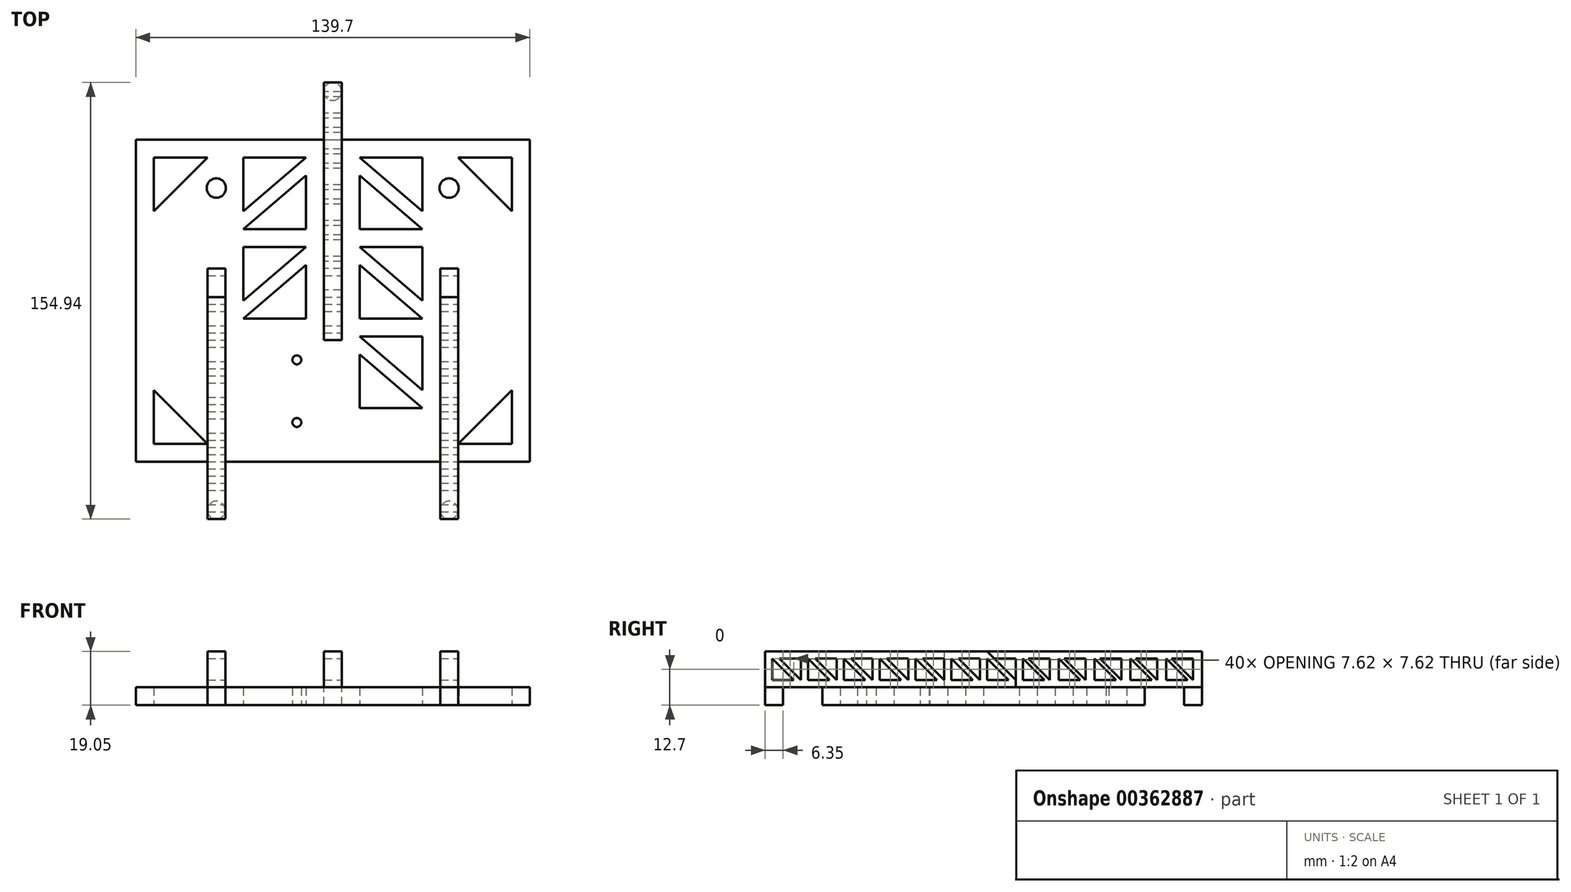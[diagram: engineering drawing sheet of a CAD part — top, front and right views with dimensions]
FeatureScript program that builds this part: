
annotation { "Feature Type Name" : "Feature", "Feature Type Description" : "" }
export const myFeature = defineFeature(function(context is Context, id is Id, definition is map)
    precondition{}
    {
        {
            var Q0;
            Q0=qCreatedBy(makeId("Top.planeOp"),FACE);
            var sketch = newSketch(context, id + "F0", { "sketchPlane" : qUnion([Q0])});
            skLineSegment(sketch, "E0.bottom", {"start": v(-69.85, 57.15) * mm, "end": v(69.85, 57.15) * mm});
            skLineSegment(sketch, "E0.top", {"start": v(-69.85, -57.15) * mm, "end": v(69.85, -57.15) * mm});
            skLineSegment(sketch, "E0.left", {"start": v(-69.85, 57.15) * mm, "end": v(-69.85, -57.15) * mm});
            skLineSegment(sketch, "E0.right", {"start": v(69.85, 57.15) * mm, "end": v(69.85, -57.15) * mm});
            skPoint(sketch, "E0.middle", {"position": v(0, 0) * mm});
            skCircle(sketch, "E1", {"center": v(-41.28, 40) * mm, "radius": 3.43 * mm});
            skCircle(sketch, "E2.MirrorC", {"center": v(41.28, 40) * mm, "radius": 3.43 * mm});
            skCircle(sketch, "E3", {"center": v(-12.7, -43.18) * mm, "radius": 1.59 * mm});
            skCircle(sketch, "E4", {"center": v(-12.7, -20.95) * mm, "radius": 1.59 * mm});
            skLineSegment(sketch, "E5", {"start": v(-63.5, 50.8) * mm, "end": v(-63.5, 31.75) * mm});
            skLineSegment(sketch, "E6", {"start": v(-63.5, 31.75) * mm, "end": v(-44.45, 50.8) * mm});
            skLineSegment(sketch, "E7", {"start": v(-44.45, 50.8) * mm, "end": v(-63.5, 50.8) * mm});
            skLineSegment(sketch, "E8.MirrorCS", {"start": v(63.5, 50.8) * mm, "end": v(63.5, 31.75) * mm});
            skLineSegment(sketch, "E9.MirrorCS", {"start": v(44.45, 50.8) * mm, "end": v(63.5, 50.8) * mm});
            skLineSegment(sketch, "E10.MirrorCS", {"start": v(63.5, 31.75) * mm, "end": v(44.45, 50.8) * mm});
            skLineSegment(sketch, "E11.MirrorCS", {"start": v(-63.5, -50.8) * mm, "end": v(-63.5, -31.75) * mm});
            skLineSegment(sketch, "E12.MirrorCS", {"start": v(-63.5, -31.75) * mm, "end": v(-44.45, -50.8) * mm});
            skLineSegment(sketch, "E13.MirrorCS", {"start": v(-44.45, -50.8) * mm, "end": v(-63.5, -50.8) * mm});
            skLineSegment(sketch, "E14.MirrorCS", {"start": v(44.45, -50.8) * mm, "end": v(63.5, -50.8) * mm});
            skLineSegment(sketch, "E15.MirrorCS", {"start": v(63.5, -31.75) * mm, "end": v(44.45, -50.8) * mm});
            skLineSegment(sketch, "E16.MirrorCS", {"start": v(63.5, -50.8) * mm, "end": v(63.5, -31.75) * mm});
            skLineSegment(sketch, "E17", {"start": v(-31.75, 50.8) * mm, "end": v(-31.75, 31.75) * mm});
            skLineSegment(sketch, "E18", {"start": v(-31.75, 31.75) * mm, "end": v(-9.53, 50.8) * mm});
            skLineSegment(sketch, "E19", {"start": v(-9.52, 50.8) * mm, "end": v(-31.75, 50.8) * mm});
            skLineSegment(sketch, "E20", {"start": v(-31.75, 25.4) * mm, "end": v(-9.52, 44.45) * mm});
            skLineSegment(sketch, "E21", {"start": v(-9.53, 44.45) * mm, "end": v(-9.53, 25.4) * mm});
            skLineSegment(sketch, "E22", {"start": v(-9.52, 25.4) * mm, "end": v(-31.75, 25.4) * mm});
            skLineSegment(sketch, "E23.0.1.0", {"start": v(-31.75, 0) * mm, "end": v(-9.53, 19.05) * mm});
            skLineSegment(sketch, "E23.0.1.1", {"start": v(-31.75, 19.05) * mm, "end": v(-31.75, 0) * mm});
            skLineSegment(sketch, "E23.0.1.2", {"start": v(-9.52, 19.05) * mm, "end": v(-31.75, 19.05) * mm});
            skLineSegment(sketch, "E23.0.1.3", {"start": v(-31.75, -6.35) * mm, "end": v(-9.52, 12.7) * mm});
            skLineSegment(sketch, "E23.0.1.4", {"start": v(-9.53, 12.7) * mm, "end": v(-9.53, -6.35) * mm});
            skLineSegment(sketch, "E23.0.1.5", {"start": v(-9.52, -6.35) * mm, "end": v(-31.75, -6.35) * mm});
            skLineSegment(sketch, "E23.direction1", {"start": v(-31.75, 31.75) * mm, "end": v(-6.35, 31.75) * mm, "construction": true});
            skLineSegment(sketch, "E23.direction2", {"start": v(-31.75, 31.75) * mm, "end": v(-31.75, 0) * mm, "construction": true});
            skLineSegment(sketch, "E24.MirrorCS", {"start": v(31.75, 31.75) * mm, "end": v(9.53, 50.8) * mm});
            skLineSegment(sketch, "E25.MirrorCS", {"start": v(31.75, 50.8) * mm, "end": v(31.75, 31.75) * mm});
            skLineSegment(sketch, "E26.MirrorCS", {"start": v(9.52, 50.8) * mm, "end": v(31.75, 50.8) * mm});
            skLineSegment(sketch, "E27.MirrorCS", {"start": v(31.75, 25.4) * mm, "end": v(9.52, 44.45) * mm});
            skLineSegment(sketch, "E28.MirrorCS", {"start": v(9.53, 44.45) * mm, "end": v(9.53, 25.4) * mm});
            skLineSegment(sketch, "E29.MirrorCS", {"start": v(9.52, 25.4) * mm, "end": v(31.75, 25.4) * mm});
            skLineSegment(sketch, "E30.0.1.0", {"start": v(31.75, -6.35) * mm, "end": v(9.52, 12.7) * mm});
            skLineSegment(sketch, "E30.0.1.1", {"start": v(9.53, 12.7) * mm, "end": v(9.53, -6.35) * mm});
            skLineSegment(sketch, "E30.0.1.2", {"start": v(9.52, -6.35) * mm, "end": v(31.75, -6.35) * mm});
            skLineSegment(sketch, "E30.0.1.3", {"start": v(31.75, 0) * mm, "end": v(9.53, 19.05) * mm});
            skLineSegment(sketch, "E30.0.1.4", {"start": v(9.52, 19.05) * mm, "end": v(31.75, 19.05) * mm});
            skLineSegment(sketch, "E30.0.1.5", {"start": v(31.75, 19.05) * mm, "end": v(31.75, 0) * mm});
            skLineSegment(sketch, "E30.0.2.0", {"start": v(31.75, -38.1) * mm, "end": v(9.52, -19.05) * mm});
            skLineSegment(sketch, "E30.0.2.1", {"start": v(9.53, -19.05) * mm, "end": v(9.53, -38.1) * mm});
            skLineSegment(sketch, "E30.0.2.2", {"start": v(9.52, -38.1) * mm, "end": v(31.75, -38.1) * mm});
            skLineSegment(sketch, "E30.0.2.3", {"start": v(31.75, -31.75) * mm, "end": v(9.53, -12.7) * mm});
            skLineSegment(sketch, "E30.0.2.4", {"start": v(9.52, -12.7) * mm, "end": v(31.75, -12.7) * mm});
            skLineSegment(sketch, "E30.0.2.5", {"start": v(31.75, -12.7) * mm, "end": v(31.75, -31.75) * mm});
            skLineSegment(sketch, "E30.direction1", {"start": v(9.52, 25.4) * mm, "end": v(34.92, 25.4) * mm, "construction": true});
            skLineSegment(sketch, "E30.direction2", {"start": v(9.52, 25.4) * mm, "end": v(9.52, -6.35) * mm, "construction": true});
            skSolve(sketch);
        }
        {
            var Q0;
            Q0=makeQuery(id+"F0.imprint","IMPRINT",FACE,{"disambiguationData":[TD([[makeQuery(id+"F0.imprint","IMPRINT",EDGE,{"derivedFrom":sQuery(id+"F0.wireOp",EDGE,"E0.bottom")}),-1.0]])]});
            extrude(context, id + "F1", {"entities" : qUnion([Q0]), "depth" : 6.35 * mm});
        }
        {
            var Q0;
            Q0=makeQuery(id+"F1.opExtrude","CAP_FACE",FACE,{"disambiguationData":[OSD([sQuery(id+"F0.wireOp",EDGE,"E0.bottom"),sQuery(id+"F0.wireOp",EDGE,"E0.top"),sQuery(id+"F0.wireOp",EDGE,"E0.left"),sQuery(id+"F0.wireOp",EDGE,"E0.right"),sQuery(id+"F0.wireOp",EDGE,"E1"),sQuery(id+"F0.wireOp",EDGE,"E2.MirrorC")])],"isStart":false});
            var sketch = newSketch(context, id + "F2", { "sketchPlane" : qUnion([Q0])});
            skLineSegment(sketch, "E31.bottom", {"start": v(-38.1, -77.47) * mm, "end": v(-44.45, -77.47) * mm});
            skLineSegment(sketch, "E31.top", {"start": v(-38.1, 11.43) * mm, "end": v(-44.45, 11.43) * mm});
            skLineSegment(sketch, "E31.left", {"start": v(-38.1, -77.47) * mm, "end": v(-38.1, 11.43) * mm});
            skLineSegment(sketch, "E31.right", {"start": v(-44.45, -77.47) * mm, "end": v(-44.45, 11.43) * mm});
            skPoint(sketch, "E31.middle", {"position": v(-41.27, -33.02) * mm});
            skLineSegment(sketch, "E32.MirrorCS", {"start": v(44.45, -77.47) * mm, "end": v(44.45, 11.43) * mm});
            skLineSegment(sketch, "E33.MirrorCS", {"start": v(38.1, -77.47) * mm, "end": v(38.1, 11.43) * mm});
            skLineSegment(sketch, "E34.MirrorCS", {"start": v(38.1, 11.43) * mm, "end": v(44.45, 11.43) * mm});
            skLineSegment(sketch, "E35.MirrorCS", {"start": v(38.1, -77.47) * mm, "end": v(44.45, -77.47) * mm});
            skLineSegment(sketch, "E36.bottom", {"start": v(-3.17, 77.47) * mm, "end": v(3.18, 77.47) * mm});
            skLineSegment(sketch, "E36.top", {"start": v(-3.17, -13.97) * mm, "end": v(3.18, -13.97) * mm});
            skLineSegment(sketch, "E36.left", {"start": v(-3.17, 77.47) * mm, "end": v(-3.17, -13.97) * mm});
            skLineSegment(sketch, "E36.right", {"start": v(3.18, 77.47) * mm, "end": v(3.18, -13.97) * mm});
            skPoint(sketch, "E36.middle", {"position": v(0, 31.75) * mm});
            skSolve(sketch);
        }
        {
            var Q0;
            {var subQ0=sQuery(id+"F2.wireOp",EDGE,"E31.top");Q0=makeQuery(id+"F2.imprint","IMPRINT",FACE,{"disambiguationData":[TD([[makeQuery(id+"F2.imprint","IMPRINT",EDGE,{"derivedFrom":subQ0}),1.0]])]});}
            var Q1;
            {var subQ0=sQuery(id+"F2.wireOp",EDGE,"E31.bottom");Q1=makeQuery(id+"F2.imprint","IMPRINT",FACE,{"disambiguationData":[TD([[makeQuery(id+"F2.imprint","IMPRINT",EDGE,{"derivedFrom":subQ0}),-1.0]])]});}
            var Q2;
            {var subQ0=sQuery(id+"F2.wireOp",EDGE,"E35.MirrorCS");Q2=makeQuery(id+"F2.imprint","IMPRINT",FACE,{"disambiguationData":[TD([[makeQuery(id+"F2.imprint","IMPRINT",EDGE,{"derivedFrom":subQ0}),1.0]])]});}
            var Q3;
            {var subQ0=sQuery(id+"F2.wireOp",EDGE,"E34.MirrorCS");Q3=makeQuery(id+"F2.imprint","IMPRINT",FACE,{"disambiguationData":[TD([[makeQuery(id+"F2.imprint","IMPRINT",EDGE,{"derivedFrom":subQ0}),-1.0]])]});}
            var Q4;
            {var subQ0=sQuery(id+"F2.wireOp",EDGE,"E36.top");Q4=makeQuery(id+"F2.imprint","IMPRINT",FACE,{"disambiguationData":[TD([[makeQuery(id+"F2.imprint","IMPRINT",EDGE,{"derivedFrom":subQ0}),1.0]])]});}
            var Q5;
            {var subQ0=sQuery(id+"F2.wireOp",EDGE,"E36.bottom");Q5=makeQuery(id+"F2.imprint","IMPRINT",FACE,{"disambiguationData":[TD([[makeQuery(id+"F2.imprint","IMPRINT",EDGE,{"derivedFrom":subQ0}),-1.0]])]});}
            extrude(context, id + "F3", {"entities" : qUnion([Q0, Q1, Q2, Q3, Q4, Q5]), "operationType" : NewBodyOperationType.ADD, "depth" : 12.7 * mm});
        }
        {
            var Q0;
            Q0=makeQuery(id+"F3.opExtrude","CAP_FACE",FACE,{"disambiguationData":[OSD([sQuery(id+"F2.wireOp",EDGE,"E31.bottom"),sQuery(id+"F2.wireOp",EDGE,"E31.top"),sQuery(id+"F2.wireOp",EDGE,"E31.left"),sQuery(id+"F2.wireOp",EDGE,"E31.right")])],"isStart":true});
            var sketch = newSketch(context, id + "F4", { "sketchPlane" : qUnion([Q0])});
            skCircle(sketch, "E37", {"center": v(-41.27, 74.3) * mm, "radius": 3.18 * mm});
            skCircle(sketch, "E38", {"center": v(41.27, 74.3) * mm, "radius": 3.18 * mm});
            skCircle(sketch, "E39", {"center": v(0, -74.3) * mm, "radius": 3.18 * mm});
            skSolve(sketch);
        }
        {
            var Q0;
            {var subQ0=sQuery(id+"F4.wireOp",EDGE,"E37");var subQ1=sQuery(id+"F2.wireOp",EDGE,"E31.bottom");var subQ2=makeQuery(id+"F4.imprint","INTERSECT",VERTEX,{"derivedFrom":[makeQuery(id+"F3.opExtrude","CAP_EDGE",EDGE,{"disambiguationData":[OSD([subQ1])],"isStart":true}),subQ0]});Q0=makeQuery(id+"F4.imprint","IMPRINT",FACE,{"disambiguationData":[TD([[makeQuery(id+"F4.imprint","IMPRINT",EDGE,{"disambiguationData":[TD([[subQ2,1.0]])],"derivedFrom":subQ0}),1.0]])]});}
            var Q1;
            Q1=makeQuery(id+"F4.imprint","IMPRINT",FACE,{"disambiguationData":[TD([[makeQuery(id+"F4.imprint","IMPRINT",EDGE,{"derivedFrom":sQuery(id+"F4.wireOp",EDGE,"E38")}),1.0]])]});
            var Q2;
            Q2=makeQuery(id+"F4.imprint","IMPRINT",FACE,{"disambiguationData":[TD([[makeQuery(id+"F4.imprint","IMPRINT",EDGE,{"derivedFrom":sQuery(id+"F4.wireOp",EDGE,"E39")}),1.0]])]});
            extrude(context, id + "F5", {"entities" : qUnion([Q0, Q1, Q2]), "operationType" : NewBodyOperationType.ADD, "depth" : 6.35 * mm});
        }
        {
            var Q0;
            Q0=makeQuery(id+"F3.opExtrude","SWEPT_FACE",FACE,{"disambiguationData":[OSD([sQuery(id+"F2.wireOp",EDGE,"E32.MirrorCS")])]});
            var sketch = newSketch(context, id + "F6", { "sketchPlane" : qUnion([Q0])});
            skLineSegment(sketch, "E40", {"start": v(-74.93, 16.51) * mm, "end": v(-74.93, 8.89) * mm});
            skLineSegment(sketch, "E41", {"start": v(-74.93, 8.89) * mm, "end": v(-67.31, 8.89) * mm});
            skLineSegment(sketch, "E42", {"start": v(-67.31, 8.89) * mm, "end": v(-74.93, 16.5) * mm});
            skLineSegment(sketch, "E43", {"start": v(-72.4, 16.51) * mm, "end": v(-64.77, 8.89) * mm});
            skLineSegment(sketch, "E44", {"start": v(-64.77, 8.9) * mm, "end": v(-64.77, 16.51) * mm});
            skLineSegment(sketch, "E45", {"start": v(-64.77, 16.5) * mm, "end": v(-72.4, 16.5) * mm});
            skLineSegment(sketch, "E46.1.0.0", {"start": v(-52.07, 8.9) * mm, "end": v(-52.07, 16.51) * mm});
            skLineSegment(sketch, "E46.1.0.1", {"start": v(-59.7, 16.51) * mm, "end": v(-52.07, 8.9) * mm});
            skLineSegment(sketch, "E46.1.0.2", {"start": v(-52.07, 16.5) * mm, "end": v(-59.7, 16.5) * mm});
            skLineSegment(sketch, "E46.1.0.3", {"start": v(-54.61, 8.89) * mm, "end": v(-62.23, 16.5) * mm});
            skLineSegment(sketch, "E46.1.0.4", {"start": v(-62.23, 16.51) * mm, "end": v(-62.23, 8.89) * mm});
            skLineSegment(sketch, "E46.1.0.5", {"start": v(-62.23, 8.89) * mm, "end": v(-54.61, 8.89) * mm});
            skLineSegment(sketch, "E46.2.0.0", {"start": v(-39.37, 8.9) * mm, "end": v(-39.37, 16.51) * mm});
            skLineSegment(sketch, "E46.2.0.1", {"start": v(-47, 16.51) * mm, "end": v(-39.37, 8.9) * mm});
            skLineSegment(sketch, "E46.2.0.2", {"start": v(-39.37, 16.5) * mm, "end": v(-47, 16.5) * mm});
            skLineSegment(sketch, "E46.2.0.3", {"start": v(-41.91, 8.89) * mm, "end": v(-49.53, 16.5) * mm});
            skLineSegment(sketch, "E46.2.0.4", {"start": v(-49.53, 16.51) * mm, "end": v(-49.53, 8.89) * mm});
            skLineSegment(sketch, "E46.2.0.5", {"start": v(-49.53, 8.89) * mm, "end": v(-41.91, 8.89) * mm});
            skLineSegment(sketch, "E46.3.0.0", {"start": v(-26.67, 8.9) * mm, "end": v(-26.67, 16.51) * mm});
            skLineSegment(sketch, "E46.3.0.1", {"start": v(-34.3, 16.51) * mm, "end": v(-26.67, 8.9) * mm});
            skLineSegment(sketch, "E46.3.0.2", {"start": v(-26.67, 16.5) * mm, "end": v(-34.3, 16.5) * mm});
            skLineSegment(sketch, "E46.3.0.3", {"start": v(-29.21, 8.89) * mm, "end": v(-36.83, 16.5) * mm});
            skLineSegment(sketch, "E46.3.0.4", {"start": v(-36.83, 16.51) * mm, "end": v(-36.83, 8.89) * mm});
            skLineSegment(sketch, "E46.3.0.5", {"start": v(-36.83, 8.89) * mm, "end": v(-29.21, 8.89) * mm});
            skLineSegment(sketch, "E46.4.0.0", {"start": v(-13.97, 8.9) * mm, "end": v(-13.97, 16.51) * mm});
            skLineSegment(sketch, "E46.4.0.1", {"start": v(-21.59, 16.51) * mm, "end": v(-13.97, 8.9) * mm});
            skLineSegment(sketch, "E46.4.0.2", {"start": v(-13.97, 16.5) * mm, "end": v(-21.59, 16.5) * mm});
            skLineSegment(sketch, "E46.4.0.3", {"start": v(-16.51, 8.89) * mm, "end": v(-24.13, 16.5) * mm});
            skLineSegment(sketch, "E46.4.0.4", {"start": v(-24.13, 16.51) * mm, "end": v(-24.13, 8.89) * mm});
            skLineSegment(sketch, "E46.4.0.5", {"start": v(-24.13, 8.89) * mm, "end": v(-16.5, 8.89) * mm});
            skLineSegment(sketch, "E46.5.0.0", {"start": v(-1.27, 8.9) * mm, "end": v(-1.27, 16.51) * mm});
            skLineSegment(sketch, "E46.5.0.1", {"start": v(-8.89, 16.51) * mm, "end": v(-1.27, 8.9) * mm});
            skLineSegment(sketch, "E46.5.0.2", {"start": v(-1.27, 16.5) * mm, "end": v(-8.89, 16.5) * mm});
            skLineSegment(sketch, "E46.5.0.3", {"start": v(-3.81, 8.89) * mm, "end": v(-11.43, 16.5) * mm});
            skLineSegment(sketch, "E46.5.0.4", {"start": v(-11.43, 16.51) * mm, "end": v(-11.43, 8.89) * mm});
            skLineSegment(sketch, "E46.5.0.5", {"start": v(-11.43, 8.89) * mm, "end": v(-3.8, 8.89) * mm});
            skLineSegment(sketch, "E46.direction1", {"start": v(-64.77, 8.9) * mm, "end": v(-52.07, 8.9) * mm, "construction": true});
            skLineSegment(sketch, "E47", {"start": v(1.27, 16.51) * mm, "end": v(1.27, 8.89) * mm});
            skLineSegment(sketch, "E48", {"start": v(1.27, 8.9) * mm, "end": v(8.9, 8.9) * mm});
            skLineSegment(sketch, "E49", {"start": v(8.9, 8.9) * mm, "end": v(1.27, 16.51) * mm});
            skSolve(sketch);
        }
        {
            var Q0;
            Q0=makeQuery(id+"F3.opExtrude","CAP_EDGE",EDGE,{"disambiguationData":[OSD([sQuery(id+"F2.wireOp",EDGE,"E34.MirrorCS")])],"isStart":false});
            var Q1;
            Q1=makeQuery(id+"F3.opExtrude","CAP_EDGE",EDGE,{"disambiguationData":[OSD([sQuery(id+"F2.wireOp",EDGE,"E31.top")])],"isStart":false});
            chamfer(context, id + "F7", {"entities" : qUnion([Q0, Q1]), "width" : 10.16 * mm, "tangentPropagation" : true});
        }
        {
            var Q0;
            Q0=makeQuery(id+"F6.imprint","IMPRINT",FACE,{"disambiguationData":[TD([[makeQuery(id+"F6.imprint","IMPRINT",EDGE,{"derivedFrom":sQuery(id+"F6.wireOp",EDGE,"E40")}),1.0]])]});
            var Q1;
            Q1=makeQuery(id+"F6.imprint","IMPRINT",FACE,{"disambiguationData":[TD([[makeQuery(id+"F6.imprint","IMPRINT",EDGE,{"derivedFrom":sQuery(id+"F6.wireOp",EDGE,"E43")}),1.0]])]});
            var Q2;
            Q2=makeQuery(id+"F6.imprint","IMPRINT",FACE,{"disambiguationData":[TD([[makeQuery(id+"F6.imprint","IMPRINT",EDGE,{"derivedFrom":sQuery(id+"F6.wireOp",EDGE,"E46.1.0.3")}),1.0]])]});
            var Q3;
            Q3=makeQuery(id+"F6.imprint","IMPRINT",FACE,{"disambiguationData":[TD([[makeQuery(id+"F6.imprint","IMPRINT",EDGE,{"derivedFrom":sQuery(id+"F6.wireOp",EDGE,"E46.1.0.0")}),1.0]])]});
            var Q4;
            Q4=makeQuery(id+"F6.imprint","IMPRINT",FACE,{"disambiguationData":[TD([[makeQuery(id+"F6.imprint","IMPRINT",EDGE,{"derivedFrom":sQuery(id+"F6.wireOp",EDGE,"E46.2.0.3")}),1.0]])]});
            var Q5;
            Q5=makeQuery(id+"F6.imprint","IMPRINT",FACE,{"disambiguationData":[TD([[makeQuery(id+"F6.imprint","IMPRINT",EDGE,{"derivedFrom":sQuery(id+"F6.wireOp",EDGE,"E46.2.0.0")}),1.0]])]});
            var Q6;
            Q6=makeQuery(id+"F6.imprint","IMPRINT",FACE,{"disambiguationData":[TD([[makeQuery(id+"F6.imprint","IMPRINT",EDGE,{"derivedFrom":sQuery(id+"F6.wireOp",EDGE,"E46.3.0.3")}),1.0]])]});
            var Q7;
            Q7=makeQuery(id+"F6.imprint","IMPRINT",FACE,{"disambiguationData":[TD([[makeQuery(id+"F6.imprint","IMPRINT",EDGE,{"derivedFrom":sQuery(id+"F6.wireOp",EDGE,"E46.3.0.0")}),1.0]])]});
            var Q8;
            Q8=makeQuery(id+"F6.imprint","IMPRINT",FACE,{"disambiguationData":[TD([[makeQuery(id+"F6.imprint","IMPRINT",EDGE,{"derivedFrom":sQuery(id+"F6.wireOp",EDGE,"E46.4.0.3")}),1.0]])]});
            var Q9;
            Q9=makeQuery(id+"F6.imprint","IMPRINT",FACE,{"disambiguationData":[TD([[makeQuery(id+"F6.imprint","IMPRINT",EDGE,{"derivedFrom":sQuery(id+"F6.wireOp",EDGE,"E46.4.0.0")}),1.0]])]});
            var Q10;
            Q10=makeQuery(id+"F6.imprint","IMPRINT",FACE,{"disambiguationData":[TD([[makeQuery(id+"F6.imprint","IMPRINT",EDGE,{"derivedFrom":sQuery(id+"F6.wireOp",EDGE,"E46.5.0.3")}),1.0]])]});
            var Q11;
            Q11=makeQuery(id+"F6.imprint","IMPRINT",FACE,{"disambiguationData":[TD([[makeQuery(id+"F6.imprint","IMPRINT",EDGE,{"derivedFrom":sQuery(id+"F6.wireOp",EDGE,"E46.5.0.0")}),1.0]])]});
            var Q12;
            Q12=makeQuery(id+"F6.imprint","IMPRINT",FACE,{"disambiguationData":[TD([[makeQuery(id+"F6.imprint","IMPRINT",EDGE,{"derivedFrom":sQuery(id+"F6.wireOp",EDGE,"E47")}),1.0]])]});
            extrude(context, id + "F8", {"entities" : qUnion([Q0, Q1, Q2, Q3, Q4, Q5, Q6, Q7, Q8, Q9, Q10, Q11, Q12]), "operationType" : NewBodyOperationType.REMOVE, "endBound" : BoundingType.THROUGH_ALL, "oppositeDirection" : true, "depth" : 25.4 * mm});
        }
        {
            var Q0;
            Q0=makeQuery(id+"F3.opExtrude","SWEPT_FACE",FACE,{"disambiguationData":[OSD([sQuery(id+"F2.wireOp",EDGE,"E36.left")])]});
            var sketch = newSketch(context, id + "F9", { "sketchPlane" : qUnion([Q0])});
            skLineSegment(sketch, "E50", {"start": v(-3.81, 16.51) * mm, "end": v(-11.43, 8.9) * mm});
            skLineSegment(sketch, "E51", {"start": v(-11.43, 8.9) * mm, "end": v(-11.43, 16.51) * mm});
            skLineSegment(sketch, "E52", {"start": v(-11.43, 16.51) * mm, "end": v(-3.81, 16.51) * mm});
            skLineSegment(sketch, "E53", {"start": v(-13.97, 16.51) * mm, "end": v(-13.97, 8.9) * mm});
            skLineSegment(sketch, "E54", {"start": v(-13.97, 8.9) * mm, "end": v(-21.6, 8.9) * mm});
            skLineSegment(sketch, "E55", {"start": v(-21.6, 8.9) * mm, "end": v(-13.97, 16.51) * mm});
            skLineSegment(sketch, "E56", {"start": v(-15.8, 16.51) * mm, "end": v(-23.43, 8.9) * mm});
            skLineSegment(sketch, "E57", {"start": v(-23.43, 8.9) * mm, "end": v(-23.43, 16.51) * mm});
            skLineSegment(sketch, "E58", {"start": v(-23.43, 16.51) * mm, "end": v(-15.8, 16.51) * mm});
            skLineSegment(sketch, "E59.1.0.0", {"start": v(-36.13, 16.51) * mm, "end": v(-28.5, 16.51) * mm});
            skLineSegment(sketch, "E59.1.0.1", {"start": v(-36.13, 8.9) * mm, "end": v(-36.13, 16.51) * mm});
            skLineSegment(sketch, "E59.1.0.2", {"start": v(-28.5, 16.51) * mm, "end": v(-36.13, 8.9) * mm});
            skLineSegment(sketch, "E59.1.0.3", {"start": v(-34.3, 8.9) * mm, "end": v(-26.67, 16.51) * mm});
            skLineSegment(sketch, "E59.1.0.4", {"start": v(-26.67, 16.51) * mm, "end": v(-26.67, 8.9) * mm});
            skLineSegment(sketch, "E59.1.0.5", {"start": v(-26.67, 8.9) * mm, "end": v(-34.3, 8.9) * mm});
            skLineSegment(sketch, "E59.2.0.0", {"start": v(-48.83, 16.51) * mm, "end": v(-41.2, 16.51) * mm});
            skLineSegment(sketch, "E59.2.0.1", {"start": v(-48.83, 8.9) * mm, "end": v(-48.83, 16.51) * mm});
            skLineSegment(sketch, "E59.2.0.2", {"start": v(-41.2, 16.51) * mm, "end": v(-48.83, 8.9) * mm});
            skLineSegment(sketch, "E59.2.0.3", {"start": v(-47, 8.9) * mm, "end": v(-39.37, 16.51) * mm});
            skLineSegment(sketch, "E59.2.0.4", {"start": v(-39.37, 16.51) * mm, "end": v(-39.37, 8.9) * mm});
            skLineSegment(sketch, "E59.2.0.5", {"start": v(-39.37, 8.9) * mm, "end": v(-47, 8.9) * mm});
            skLineSegment(sketch, "E59.3.0.0", {"start": v(-61.53, 16.51) * mm, "end": v(-53.9, 16.51) * mm});
            skLineSegment(sketch, "E59.3.0.1", {"start": v(-61.53, 8.9) * mm, "end": v(-61.53, 16.51) * mm});
            skLineSegment(sketch, "E59.3.0.2", {"start": v(-53.9, 16.51) * mm, "end": v(-61.53, 8.9) * mm});
            skLineSegment(sketch, "E59.3.0.3", {"start": v(-59.69, 8.9) * mm, "end": v(-52.07, 16.51) * mm});
            skLineSegment(sketch, "E59.3.0.4", {"start": v(-52.07, 16.51) * mm, "end": v(-52.07, 8.9) * mm});
            skLineSegment(sketch, "E59.3.0.5", {"start": v(-52.07, 8.9) * mm, "end": v(-59.7, 8.9) * mm});
            skLineSegment(sketch, "E59.4.0.0", {"start": v(-74.23, 16.51) * mm, "end": v(-66.6, 16.51) * mm});
            skLineSegment(sketch, "E59.4.0.1", {"start": v(-74.23, 8.9) * mm, "end": v(-74.23, 16.51) * mm});
            skLineSegment(sketch, "E59.4.0.2", {"start": v(-66.6, 16.51) * mm, "end": v(-74.23, 8.9) * mm});
            skLineSegment(sketch, "E59.4.0.3", {"start": v(-72.4, 8.89) * mm, "end": v(-64.77, 16.51) * mm});
            skLineSegment(sketch, "E59.4.0.4", {"start": v(-64.77, 16.51) * mm, "end": v(-64.77, 8.9) * mm});
            skLineSegment(sketch, "E59.4.0.5", {"start": v(-64.77, 8.9) * mm, "end": v(-72.4, 8.9) * mm});
            skLineSegment(sketch, "E59.direction1", {"start": v(-23.43, 16.51) * mm, "end": v(-36.13, 16.51) * mm, "construction": true});
            skSolve(sketch);
        }
        {
            var Q0;
            Q0=makeQuery(id+"F9.imprint","IMPRINT",FACE,{"disambiguationData":[TD([[makeQuery(id+"F9.imprint","IMPRINT",EDGE,{"derivedFrom":sQuery(id+"F9.wireOp",EDGE,"E50")}),-1.0]])]});
            var Q1;
            Q1=makeQuery(id+"F9.imprint","IMPRINT",FACE,{"disambiguationData":[TD([[makeQuery(id+"F9.imprint","IMPRINT",EDGE,{"derivedFrom":sQuery(id+"F9.wireOp",EDGE,"E53")}),-1.0]])]});
            var Q2;
            Q2=makeQuery(id+"F9.imprint","IMPRINT",FACE,{"disambiguationData":[TD([[makeQuery(id+"F9.imprint","IMPRINT",EDGE,{"derivedFrom":sQuery(id+"F9.wireOp",EDGE,"E56")}),-1.0]])]});
            var Q3;
            Q3=makeQuery(id+"F9.imprint","IMPRINT",FACE,{"disambiguationData":[TD([[makeQuery(id+"F9.imprint","IMPRINT",EDGE,{"derivedFrom":sQuery(id+"F9.wireOp",EDGE,"E59.1.0.3")}),-1.0]])]});
            var Q4;
            Q4=makeQuery(id+"F9.imprint","IMPRINT",FACE,{"disambiguationData":[TD([[makeQuery(id+"F9.imprint","IMPRINT",EDGE,{"derivedFrom":sQuery(id+"F9.wireOp",EDGE,"E59.1.0.0")}),-1.0]])]});
            var Q5;
            Q5=makeQuery(id+"F9.imprint","IMPRINT",FACE,{"disambiguationData":[TD([[makeQuery(id+"F9.imprint","IMPRINT",EDGE,{"derivedFrom":sQuery(id+"F9.wireOp",EDGE,"E59.2.0.3")}),-1.0]])]});
            var Q6;
            Q6=makeQuery(id+"F9.imprint","IMPRINT",FACE,{"disambiguationData":[TD([[makeQuery(id+"F9.imprint","IMPRINT",EDGE,{"derivedFrom":sQuery(id+"F9.wireOp",EDGE,"E59.2.0.0")}),-1.0]])]});
            var Q7;
            Q7=makeQuery(id+"F9.imprint","IMPRINT",FACE,{"disambiguationData":[TD([[makeQuery(id+"F9.imprint","IMPRINT",EDGE,{"derivedFrom":sQuery(id+"F9.wireOp",EDGE,"E59.3.0.3")}),-1.0]])]});
            var Q8;
            Q8=makeQuery(id+"F9.imprint","IMPRINT",FACE,{"disambiguationData":[TD([[makeQuery(id+"F9.imprint","IMPRINT",EDGE,{"derivedFrom":sQuery(id+"F9.wireOp",EDGE,"E59.3.0.0")}),-1.0]])]});
            var Q9;
            Q9=makeQuery(id+"F9.imprint","IMPRINT",FACE,{"disambiguationData":[TD([[makeQuery(id+"F9.imprint","IMPRINT",EDGE,{"derivedFrom":sQuery(id+"F9.wireOp",EDGE,"E59.4.0.3")}),-1.0]])]});
            var Q10;
            Q10=makeQuery(id+"F9.imprint","IMPRINT",FACE,{"disambiguationData":[TD([[makeQuery(id+"F9.imprint","IMPRINT",EDGE,{"derivedFrom":sQuery(id+"F9.wireOp",EDGE,"E59.4.0.0")}),-1.0]])]});
            extrude(context, id + "F10", {"entities" : qUnion([Q0, Q1, Q2, Q3, Q4, Q5, Q6, Q7, Q8, Q9, Q10]), "operationType" : NewBodyOperationType.REMOVE, "endBound" : BoundingType.THROUGH_ALL, "oppositeDirection" : true, "depth" : 25.4 * mm});
        }
    });
